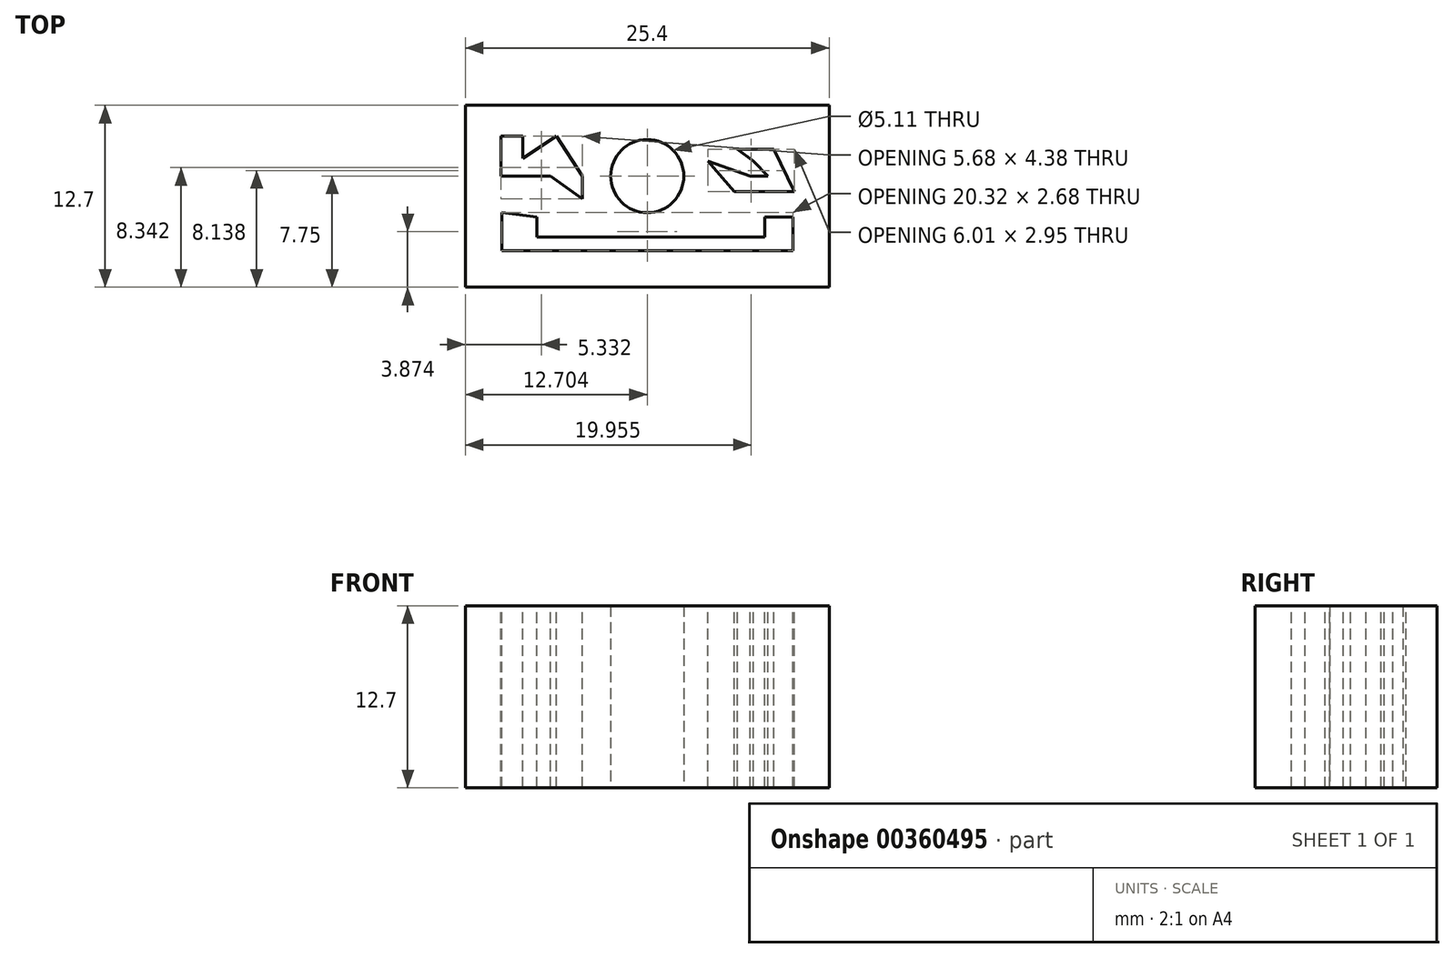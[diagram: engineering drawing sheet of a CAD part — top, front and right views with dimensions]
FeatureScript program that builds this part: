
annotation { "Feature Type Name" : "Feature", "Feature Type Description" : "" }
export const myFeature = defineFeature(function(context is Context, id is Id, definition is map)
    precondition{}
    {
        {
            var Q0;
            Q0=qCreatedBy(makeId("Top.planeOp"),FACE);
            var sketch = newSketch(context, id + "F0", { "sketchPlane" : qUnion([Q0])});
            skLineSegment(sketch, "E0.bottom", {"start": v(-12.14, 4.95) * mm, "end": v(13.26, 4.95) * mm});
            skLineSegment(sketch, "E0.top", {"start": v(-12.14, -7.75) * mm, "end": v(13.26, -7.75) * mm});
            skLineSegment(sketch, "E0.left", {"start": v(-12.14, 4.95) * mm, "end": v(-12.14, -7.75) * mm});
            skLineSegment(sketch, "E0.right", {"start": v(13.26, 4.95) * mm, "end": v(13.26, -7.75) * mm});
            skSolve(sketch);
        }
        {
            var Q0;
            Q0=makeQuery(id+"F0.imprint","IMPRINT",FACE,{"disambiguationData":[TD([[makeQuery(id+"F0.imprint","IMPRINT",EDGE,{"derivedFrom":sQuery(id+"F0.wireOp",EDGE,"E0.bottom")}),-1.0]])]});
            extrude(context, id + "F1", {"entities" : qUnion([Q0]), "depth" : 12.7 * mm});
        }
        {
            var Q0;
            Q0=qCreatedBy(makeId("Top.planeOp"),FACE);
            var sketch = newSketch(context, id + "F2", { "sketchPlane" : qUnion([Q0])});
            skCircle(sketch, "E1", {"center": v(0.56, 0) * mm, "radius": 2.54 * mm});
            skSolve(sketch);
        }
        {
            var Q0;
            Q0=sQuery(id+"F2.wireOp",VERTEX,"E1.center");
            var Q1;
            Q1=makeQuery(id+"F1.opExtrude","SWEPT_BODY",BODY,{"disambiguationData":[OSD([sQuery(id+"F0.wireOp",EDGE,"E0.bottom"),sQuery(id+"F0.wireOp",EDGE,"E0.top"),sQuery(id+"F0.wireOp",EDGE,"E0.left"),sQuery(id+"F0.wireOp",EDGE,"E0.right")])]});
            hole(context, id + "F3", {"style" : HoleStyle.SIMPLE, "endStyle" : HoleEndStyle.THROUGH, "oppositeDirection" : true, "holeDiameter" : 5.1 * mm, "isTappedThrough" : true, "tappedDepth" : 12.7 * mm, "tapClearance" : 3, "locations" : qUnion([Q0]), "scope" : qUnion([Q1])});
        }
        {
            var Q0;
            Q0=makeQuery(id+"F1.opExtrude","CAP_FACE",FACE,{"disambiguationData":[OSD([sQuery(id+"F0.wireOp",EDGE,"E0.bottom"),sQuery(id+"F0.wireOp",EDGE,"E0.top"),sQuery(id+"F0.wireOp",EDGE,"E0.left"),sQuery(id+"F0.wireOp",EDGE,"E0.right")])],"isStart":false});
            var sketch = newSketch(context, id + "F4", { "sketchPlane" : qUnion([Q0])});
            skLineSegment(sketch, "E2.top", {"start": v(-9.6, -5.21) * mm, "end": v(10.72, -5.21) * mm});
            skLineSegment(sketch, "E2.left", {"start": v(-9.6, -2.54) * mm, "end": v(-9.6, -5.21) * mm});
            skLineSegment(sketch, "E2.right", {"start": v(10.72, -2.85) * mm, "end": v(10.72, -5.21) * mm});
            skLineSegment(sketch, "E3", {"start": v(10.72, -2.85) * mm, "end": v(8.77, -2.85) * mm});
            skLineSegment(sketch, "E4", {"start": v(8.77, -2.85) * mm, "end": v(8.77, -4.25) * mm});
            skLineSegment(sketch, "E5", {"start": v(8.77, -4.25) * mm, "end": v(-7.14, -4.25) * mm});
            skLineSegment(sketch, "E6", {"start": v(-7.14, -4.25) * mm, "end": v(-7.14, -2.85) * mm});
            skLineSegment(sketch, "E7", {"start": v(-7.14, -2.85) * mm, "end": v(-9.6, -2.54) * mm});
            skSolve(sketch);
        }
        {
            var Q0;
            Q0=makeQuery(id+"F4.imprint","IMPRINT",FACE,{"disambiguationData":[TD([[makeQuery(id+"F4.imprint","IMPRINT",EDGE,{"derivedFrom":sQuery(id+"F4.wireOp",EDGE,"E2.top")}),1.0]])]});
            extrude(context, id + "F5", {"entities" : qUnion([Q0]), "operationType" : NewBodyOperationType.REMOVE, "oppositeDirection" : true, "depth" : 25.4 * mm});
        }
        {
            var Q0;
            Q0=makeQuery(id+"F1.opExtrude","CAP_FACE",FACE,{"disambiguationData":[OSD([sQuery(id+"F0.wireOp",EDGE,"E0.bottom"),sQuery(id+"F0.wireOp",EDGE,"E0.top"),sQuery(id+"F0.wireOp",EDGE,"E0.left"),sQuery(id+"F0.wireOp",EDGE,"E0.right")])],"isStart":false});
            var sketch = newSketch(context, id + "F6", { "sketchPlane" : qUnion([Q0])});
            skLineSegment(sketch, "E8.top", {"start": v(-9.65, 0) * mm, "end": v(-6.19, 0) * mm});
            skLineSegment(sketch, "E8.left", {"start": v(-9.65, 2.78) * mm, "end": v(-9.65, 0) * mm});
            skLineSegment(sketch, "E9", {"start": v(-9.65, 2.78) * mm, "end": v(-8.12, 2.78) * mm});
            skLineSegment(sketch, "E10", {"start": v(-8.12, 2.78) * mm, "end": v(-8.12, 1.25) * mm});
            skLineSegment(sketch, "E11", {"start": v(-8.12, 1.25) * mm, "end": v(-5.78, 2.78) * mm});
            skLineSegment(sketch, "E12", {"start": v(-5.78, 2.78) * mm, "end": v(-3.97, 0) * mm});
            skLineSegment(sketch, "E13", {"start": v(-3.97, 0) * mm, "end": v(-3.97, -1.6) * mm});
            skLineSegment(sketch, "E14", {"start": v(-3.97, -1.6) * mm, "end": v(-6.19, 0) * mm});
            skLineSegment(sketch, "E15", {"start": v(8.99, 2.78) * mm, "end": v(6.13, -1.4) * mm});
            skLineSegment(sketch, "E16", {"start": v(6.13, -1.4) * mm, "end": v(10.41, -1.4) * mm});
            skLineSegment(sketch, "E17", {"start": v(10.41, -1.4) * mm, "end": v(11.74, 1.36) * mm});
            skLineSegment(sketch, "E18", {"start": v(11.74, 1.36) * mm, "end": v(9.4, 0) * mm});
            skLineSegment(sketch, "E19", {"start": v(9.4, 0) * mm, "end": v(10.73, 2.78) * mm});
            skLineSegment(sketch, "E20", {"start": v(10.73, 2.78) * mm, "end": v(8.99, 2.78) * mm});
            skSolve(sketch);
        }
        {
            var Q0;
            Q0=makeQuery(id+"F6.imprint","IMPRINT",FACE,{"disambiguationData":[TD([[makeQuery(id+"F6.imprint","IMPRINT",EDGE,{"derivedFrom":sQuery(id+"F6.wireOp",EDGE,"E8.top")}),1.0]])]});
            extrude(context, id + "F7", {"entities" : qUnion([Q0]), "operationType" : NewBodyOperationType.REMOVE, "oppositeDirection" : true, "depth" : 25.4 * mm});
        }
        {
            var Q0;
            Q0=makeQuery(id+"F1.opExtrude","CAP_FACE",FACE,{"disambiguationData":[OSD([sQuery(id+"F0.wireOp",EDGE,"E0.bottom"),sQuery(id+"F0.wireOp",EDGE,"E0.top"),sQuery(id+"F0.wireOp",EDGE,"E0.left"),sQuery(id+"F0.wireOp",EDGE,"E0.right")])],"isStart":false});
            var sketch = newSketch(context, id + "F8", { "sketchPlane" : qUnion([Q0])});
            skLineSegment(sketch, "E21", {"start": v(6.85, 1.87) * mm, "end": v(9.4, 1.87) * mm});
            skLineSegment(sketch, "E22", {"start": v(9.4, 1.87) * mm, "end": v(10.82, -1.09) * mm});
            skLineSegment(sketch, "E23", {"start": v(10.82, -1.09) * mm, "end": v(6.64, -1.09) * mm});
            skLineSegment(sketch, "E24", {"start": v(6.64, -1.09) * mm, "end": v(4.81, 1.05) * mm});
            skLineSegment(sketch, "E25", {"start": v(4.81, 1.05) * mm, "end": v(7.76, 0) * mm});
            skLineSegment(sketch, "E26", {"start": v(7.76, 0) * mm, "end": v(8.99, 0) * mm});
            skLineSegment(sketch, "E27", {"start": v(8.99, 0) * mm, "end": v(7.97, 1.05) * mm});
            skLineSegment(sketch, "E28", {"start": v(7.97, 1.05) * mm, "end": v(6.85, 1.87) * mm});
            skSolve(sketch);
        }
        {
            var Q0;
            Q0=makeQuery(id+"F8.imprint","IMPRINT",FACE,{"disambiguationData":[TD([[makeQuery(id+"F8.imprint","IMPRINT",EDGE,{"derivedFrom":sQuery(id+"F8.wireOp",EDGE,"E21")}),-1.0]])]});
            extrude(context, id + "F9", {"entities" : qUnion([Q0]), "operationType" : NewBodyOperationType.REMOVE, "oppositeDirection" : true, "depth" : 25.4 * mm});
        }
    });
